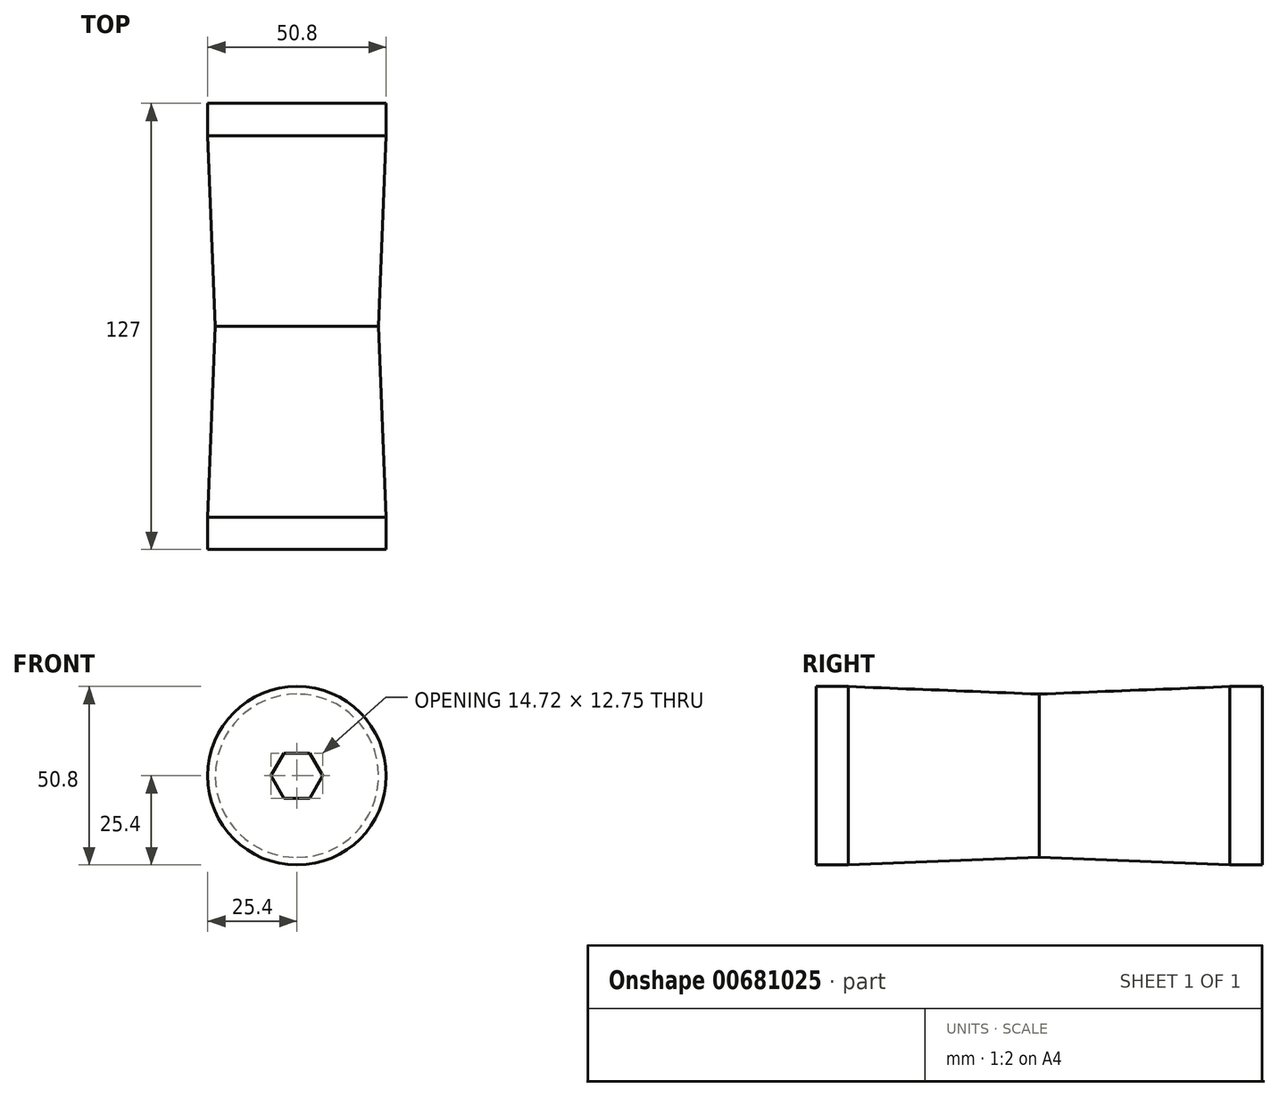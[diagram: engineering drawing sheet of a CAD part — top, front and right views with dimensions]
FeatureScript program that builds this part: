
annotation { "Feature Type Name" : "Feature", "Feature Type Description" : "" }
export const myFeature = defineFeature(function(context is Context, id is Id, definition is map)
    precondition{}
    {
        {
            var Q0;
            Q0=qCreatedBy(makeId("Front.planeOp"),FACE);
            var sketch = newSketch(context, id + "F0", { "sketchPlane" : qUnion([Q0])});
            skCircle(sketch, "E0", {"center": v(0, 0) * mm, "radius": 25.4 * mm});
            skCircle(sketch, "E1.cCircle", {"center": v(0, 0) * mm, "radius": 6.38 * mm, "construction": true});
            skLineSegment(sketch, "E1.0", {"start": v(3.68, -6.38) * mm, "end": v(-3.68, -6.38) * mm});
            skLineSegment(sketch, "E1.1", {"start": v(-3.68, -6.38) * mm, "end": v(-7.36, 0) * mm});
            skLineSegment(sketch, "E1.2", {"start": v(-7.36, 0) * mm, "end": v(-3.68, 6.38) * mm});
            skLineSegment(sketch, "E1.3", {"start": v(-3.68, 6.38) * mm, "end": v(3.68, 6.38) * mm});
            skLineSegment(sketch, "E1.4", {"start": v(3.68, 6.38) * mm, "end": v(7.36, 0) * mm});
            skLineSegment(sketch, "E1.5", {"start": v(7.36, 0) * mm, "end": v(3.68, -6.38) * mm});
            skPoint(sketch, "E1.0.midPoint", {"position": v(0, -6.38) * mm});
            skSolve(sketch);
        }
        {
            var Q0;
            Q0=makeQuery(id+"F0.imprint","IMPRINT",FACE,{"disambiguationData":[TD([[makeQuery(id+"F0.imprint","IMPRINT",EDGE,{"derivedFrom":sQuery(id+"F0.wireOp",EDGE,"E0")}),1.0]])]});
            extrude(context, id + "F1", {"entities" : qUnion([Q0]), "depth" : 63.5 * mm, "offsetDistance" : 25.4 * mm});
        }
        {
            var Q0;
            Q0=qCreatedBy(makeId("Right.planeOp"),FACE);
            var sketch = newSketch(context, id + "F2", { "sketchPlane" : qUnion([Q0])});
            skLineSegment(sketch, "E2", {"start": v(0, 0) * mm, "end": v(-63.5, 0) * mm});
            skLineSegment(sketch, "E3", {"start": v(-63.5, 0) * mm, "end": v(-63.5, 23.25) * mm});
            skLineSegment(sketch, "E4", {"start": v(-63.5, 23.25) * mm, "end": v(-3.98, 25.6) * mm});
            skLineSegment(sketch, "E5", {"start": v(-3.98, 25.6) * mm, "end": v(-63.5, 25.6) * mm});
            skLineSegment(sketch, "E6", {"start": v(-63.5, 25.6) * mm, "end": v(-63.5, 23.25) * mm});
            skLineSegment(sketch, "E7.MirrorCS", {"start": v(-63.5, 23.25) * mm, "end": v(-123.02, 25.6) * mm});
            skLineSegment(sketch, "E8.MirrorCS", {"start": v(-123.02, 25.6) * mm, "end": v(-63.5, 25.6) * mm});
            skSolve(sketch);
        }
        {
            var Q0;
            Q0=makeQuery(id+"F2.imprint","IMPRINT",FACE,{"disambiguationData":[TD([[makeQuery(id+"F2.imprint","IMPRINT",EDGE,{"derivedFrom":sQuery(id+"F2.wireOp",EDGE,"E4")}),1.0]])]});
            var Q1;
            Q1=sQuery(id+"F2.wireOp",EDGE,"E2");
            revolve(context, id + "F3", {"operationType" : NewBodyOperationType.REMOVE, "entities" : qUnion([Q0]), "axis" : qUnion([Q1]), "revolveType" : RevolveType.FULL, "oppositeDirection" : true});
        }
        {
            var Q0;
            Q0=makeQuery(id+"F1.opExtrude","CAP_FACE",FACE,{"disambiguationData":[OSD([sQuery(id+"F0.wireOp",EDGE,"E0"),sQuery(id+"F0.wireOp",EDGE,"E1.0"),sQuery(id+"F0.wireOp",EDGE,"E1.1"),sQuery(id+"F0.wireOp",EDGE,"E1.2"),sQuery(id+"F0.wireOp",EDGE,"E1.3"),sQuery(id+"F0.wireOp",EDGE,"E1.4"),sQuery(id+"F0.wireOp",EDGE,"E1.5")])],"isStart":false});
            cPlane(context, id + "F4", {"entities" : qUnion([Q0]), "cplaneType" : CPlaneType.OFFSET, "offset" : 0 * mm, "width" : 152.4 * mm, "height" : 152.4 * mm});
        }
        {
            var Q0;
            Q0=makeQuery(id+"F1.opExtrude","SWEPT_BODY",BODY,{"disambiguationData":[OSD([sQuery(id+"F0.wireOp",EDGE,"E0"),sQuery(id+"F0.wireOp",EDGE,"E1.0"),sQuery(id+"F0.wireOp",EDGE,"E1.1"),sQuery(id+"F0.wireOp",EDGE,"E1.2"),sQuery(id+"F0.wireOp",EDGE,"E1.3"),sQuery(id+"F0.wireOp",EDGE,"E1.4"),sQuery(id+"F0.wireOp",EDGE,"E1.5")])]});
            var Q1;
            Q1=qCreatedBy(id+"F4.planeOp",FACE);
            mirror(context, id + "F5", {"operationType" : NewBodyOperationType.ADD, "entities" : qUnion([Q0]), "mirrorPlane" : qUnion([Q1])});
        }
    });
